# Revit family: Термостатическая головка HERZ-Design-MINI, с присоединительной резьбой М 28х1.5, 9200 60
name_source: partatom
category: Rohrzubehör
revit_build: Autodesk Revit 2018 (Build: 20190510_1515(x64)
units: mm (PartAtom-declared; Revit-internal decimal feet)

## family parameters
Arbeitsebenenbasiert = Nein
Beim Laden mit Abzugskörper schneiden = Nein
Bemaßung runder Anschluss = Durchmesser verwenden
Gemeinsam genutzt = Nein
Immer vertikal = Nein
OmniClass-Nummer = 23.65.55.14
OmniClass-Titel = Valves for Liquid Services
Teiletyp = Normal

## types (1)
- Термостатическая головка HERZ-Design-MINI, с присоединительной резьбой М 28х1.5, 9200 60
    Hersteller = HERZ Armaturen Ges.m.b.H.
    S01 = 73 mm  [stored 0.239501 ft]
    S02 = 60 mm  [stored 0.19685 ft]
    URL = www.herz-armaturen.ru
    Диапазон регулирования = 6-28°C
    Диапазон регулирования с морозозащитой = 6-28°C
    Маховик = Пластик, белый
    Морозозащита = 6 °C
    Номер заказа = 1920060
    Область применения = Для монтажа на всех HERZ-клапанах, предназначенных для термостатической работы.
    Позиция морозозащиты * = Термостатическая головка с жидкостным датчиком (гидросенсором) с позицией морозозащиты и ограничением, блокировкой диапазона регулирования.
    Позиция теплового запирания "0" = Термостатическая головка с жидкостным датчиком (гидросенсором) с позициями теплового запираниия "0" и морозозащиты, с ограничением и блокировкой диапазона регулирования.
    Принцип действия = HERZ-термостатическая головка является датчиком прямого регулирования.
Изменение объема жидкости в HERZ-гидросенсоре приводит в движение шток клапана.

note: [stored X ft] marks values corroborated as IEEE doubles in the binary element streams (Revit-internal decimal feet)
